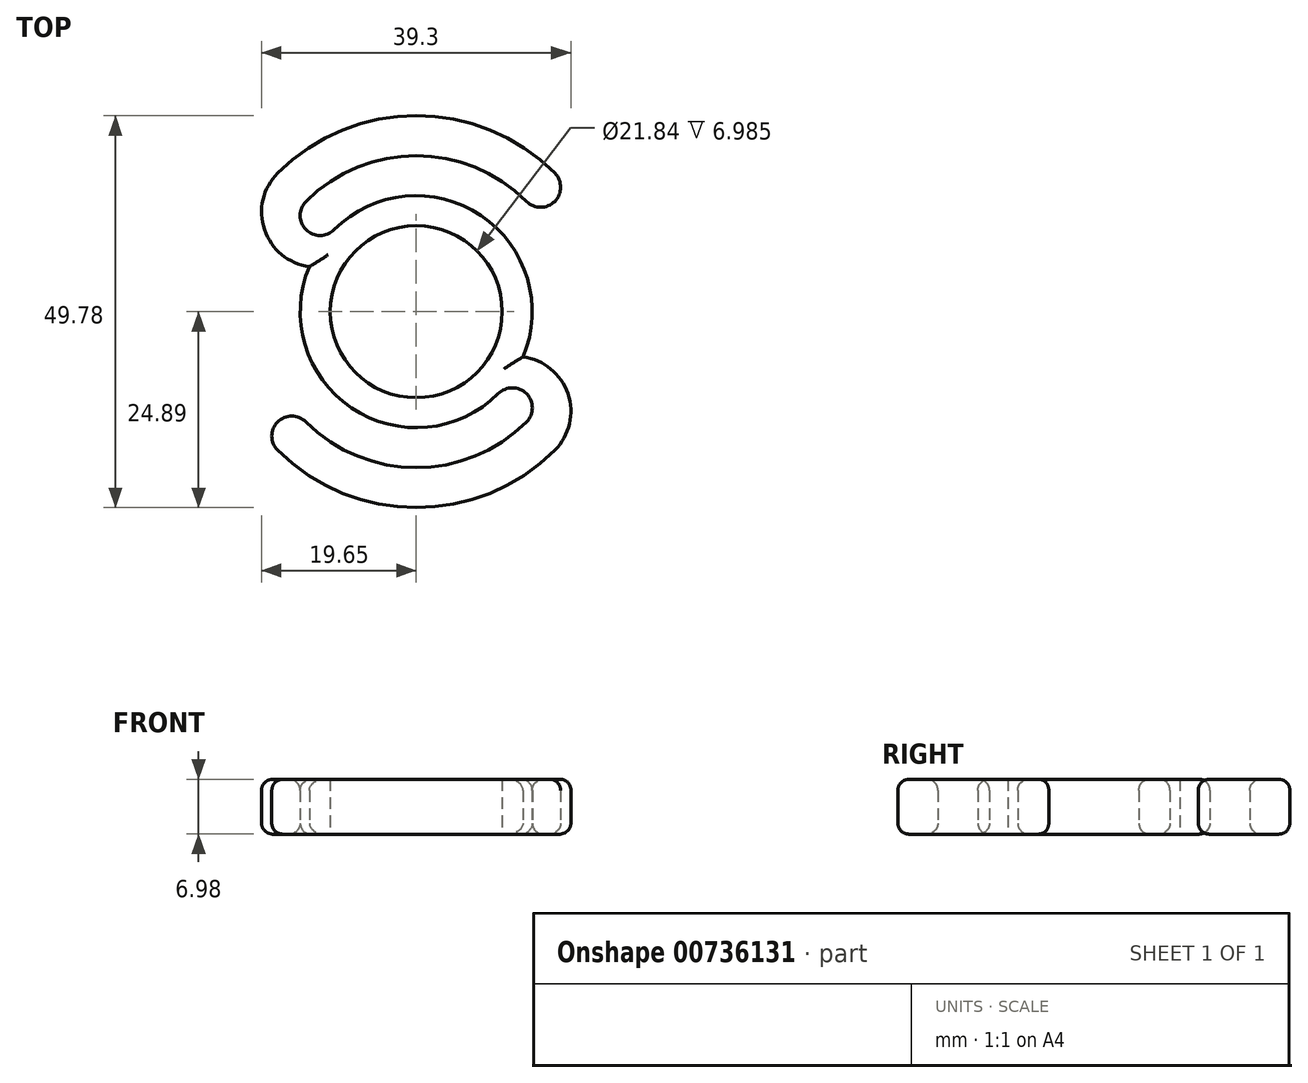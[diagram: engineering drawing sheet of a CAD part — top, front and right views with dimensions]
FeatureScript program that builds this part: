
annotation { "Feature Type Name" : "Feature", "Feature Type Description" : "" }
export const myFeature = defineFeature(function(context is Context, id is Id, definition is map)
    precondition{}
    {
        {
            var Q0;
            Q0=qCreatedBy(makeId("Top.planeOp"),FACE);
            var sketch = newSketch(context, id + "F0", { "sketchPlane" : qUnion([Q0])});
            skCircle(sketch, "E0", {"center": v(0, 0) * mm, "radius": 10.92 * mm});
            skCircle(sketch, "E1", {"center": v(0, 0) * mm, "radius": 24.9 * mm});
            skCircle(sketch, "E2", {"center": v(0, 0) * mm, "radius": 19.81 * mm});
            skLineSegment(sketch, "E3", {"start": v(0, 0) * mm, "end": v(17.6, 17.6) * mm});
            skLineSegment(sketch, "E4", {"start": v(0, 0) * mm, "end": v(-17.6, -17.6) * mm});
            skLineSegment(sketch, "E5", {"start": v(0, 0) * mm, "end": v(-17.6, 17.6) * mm});
            skLineSegment(sketch, "E6", {"start": v(0, 0) * mm, "end": v(17.6, -17.6) * mm});
            skPoint(sketch, "E7", {"position": v(14, 14) * mm});
            skPoint(sketch, "E8", {"position": v(17.6, 17.6) * mm});
            skPoint(sketch, "E9", {"position": v(15.8, 15.8) * mm});
            skCircle(sketch, "E10", {"center": v(15.8, 15.8) * mm, "radius": 2.54 * mm});
            skPoint(sketch, "E11", {"position": v(-17.6, 17.6) * mm});
            skPoint(sketch, "E12", {"position": v(-14, 14) * mm});
            skCircle(sketch, "E13", {"center": v(0, 0) * mm, "radius": 14.73 * mm});
            skPoint(sketch, "E14", {"position": v(-12.66, 12.66) * mm});
            skCircle(sketch, "E15", {"center": v(-12.66, 12.66) * mm, "radius": 6.99 * mm});
            skPoint(sketch, "E16", {"position": v(12.66, -12.66) * mm});
            skPoint(sketch, "E17", {"position": v(-15.8, -15.8) * mm});
            skCircle(sketch, "E18", {"center": v(12.66, -12.66) * mm, "radius": 6.99 * mm});
            skCircle(sketch, "E19", {"center": v(-15.8, -15.8) * mm, "radius": 2.54 * mm});
            skPoint(sketch, "E20", {"position": v(-12.21, 12.21) * mm});
            skCircle(sketch, "E21", {"center": v(-12.21, 12.21) * mm, "radius": 2.54 * mm});
            skPoint(sketch, "E22", {"position": v(12.21, -12.21) * mm});
            skCircle(sketch, "E23", {"center": v(12.21, -12.21) * mm, "radius": 2.54 * mm});
            skSolve(sketch);
        }
        {
            var Q0;
            {var subQ0=sQuery(id+"F0.wireOp",EDGE,"E10");var subQ1=sQuery(id+"F0.wireOp",EDGE,"E3");var subQ2=makeQuery(id+"F0.imprint","INTERSECT",VERTEX,{"derivedFrom":[sQuery(id+"F0.wireOp",EDGE,"E1"),subQ1,subQ0]});Q0=makeQuery(id+"F0.imprint","IMPRINT",FACE,{"disambiguationData":[TD([[makeQuery(id+"F0.imprint","IMPRINT",EDGE,{"disambiguationData":[TD([[subQ2,1.0]])],"derivedFrom":subQ1}),-1.0]])]});}
            var Q1;
            {var subQ0=sQuery(id+"F0.wireOp",EDGE,"E10");var subQ1=sQuery(id+"F0.wireOp",EDGE,"E3");var subQ2=makeQuery(id+"F0.imprint","INTERSECT",VERTEX,{"derivedFrom":[sQuery(id+"F0.wireOp",EDGE,"E1"),subQ1,subQ0]});Q1=makeQuery(id+"F0.imprint","IMPRINT",FACE,{"disambiguationData":[TD([[makeQuery(id+"F0.imprint","IMPRINT",EDGE,{"disambiguationData":[TD([[subQ2,1.0]])],"derivedFrom":subQ1}),1.0]])]});}
            var Q2;
            {var subQ4=sQuery(id+"F0.wireOp",EDGE,"E15");var subQ6=sQuery(id+"F0.wireOp",EDGE,"E2");var subQ7=makeQuery(id+"F0.imprint","INTERSECT",VERTEX,{"disambiguationData":[OD(0.0)],"derivedFrom":[subQ6,subQ4]});Q2=makeQuery(id+"F0.imprint","IMPRINT",FACE,{"disambiguationData":[TD([[makeQuery(id+"F0.imprint","IMPRINT",EDGE,{"disambiguationData":[TD([[subQ7,1.0]])],"derivedFrom":subQ6}),-1.0]])]});}
            var Q3;
            {var subQ0=sQuery(id+"F0.wireOp",EDGE,"E15");var subQ1=sQuery(id+"F0.wireOp",EDGE,"E2");var subQ2=makeQuery(id+"F0.imprint","INTERSECT",VERTEX,{"disambiguationData":[OD(0.0)],"derivedFrom":[subQ1,subQ0]});Q3=makeQuery(id+"F0.imprint","IMPRINT",FACE,{"disambiguationData":[TD([[makeQuery(id+"F0.imprint","IMPRINT",EDGE,{"disambiguationData":[TD([[subQ2,-1.0]])],"derivedFrom":subQ1}),-1.0]])]});}
            var Q4;
            {var subQ0=sQuery(id+"F0.wireOp",EDGE,"E15");var subQ1=sQuery(id+"F0.wireOp",EDGE,"E2");var subQ2=makeQuery(id+"F0.imprint","INTERSECT",VERTEX,{"disambiguationData":[OD(1.0)],"derivedFrom":[subQ1,subQ0]});Q4=makeQuery(id+"F0.imprint","IMPRINT",FACE,{"disambiguationData":[TD([[makeQuery(id+"F0.imprint","IMPRINT",EDGE,{"disambiguationData":[TD([[subQ2,1.0]])],"derivedFrom":subQ1}),-1.0]])]});}
            var Q5;
            {var subQ0=sQuery(id+"F0.wireOp",EDGE,"E15");var subQ1=sQuery(id+"F0.wireOp",EDGE,"E2");var subQ2=makeQuery(id+"F0.imprint","INTERSECT",VERTEX,{"disambiguationData":[OD(1.0)],"derivedFrom":[subQ1,subQ0]});Q5=makeQuery(id+"F0.imprint","IMPRINT",FACE,{"disambiguationData":[TD([[makeQuery(id+"F0.imprint","IMPRINT",EDGE,{"disambiguationData":[TD([[subQ2,-1.0]])],"derivedFrom":subQ0}),1.0]])]});}
            var Q6;
            {var subQ0=sQuery(id+"F0.wireOp",EDGE,"E15");var subQ3=sQuery(id+"F0.wireOp",EDGE,"E13");var subQ5=makeQuery(id+"F0.imprint","INTERSECT",VERTEX,{"disambiguationData":[OD(1.0)],"derivedFrom":[subQ3,subQ0]});Q6=makeQuery(id+"F0.imprint","IMPRINT",FACE,{"disambiguationData":[TD([[makeQuery(id+"F0.imprint","IMPRINT",EDGE,{"disambiguationData":[TD([[subQ5,1.0]])],"derivedFrom":subQ3}),1.0]])]});}
            var Q7;
            {var subQ0=sQuery(id+"F0.wireOp",EDGE,"E15");var subQ3=sQuery(id+"F0.wireOp",EDGE,"E13");var subQ5=makeQuery(id+"F0.imprint","INTERSECT",VERTEX,{"disambiguationData":[OD(0.0)],"derivedFrom":[subQ3,subQ0]});Q7=makeQuery(id+"F0.imprint","IMPRINT",FACE,{"disambiguationData":[TD([[makeQuery(id+"F0.imprint","IMPRINT",EDGE,{"disambiguationData":[TD([[subQ5,-1.0]])],"derivedFrom":subQ3}),1.0]])]});}
            var Q8;
            {var subQ0=sQuery(id+"F0.wireOp",EDGE,"E3");var subQ1=sQuery(id+"F0.wireOp",EDGE,"E0");var subQ2=makeQuery(id+"F0.imprint","INTERSECT",VERTEX,{"derivedFrom":[subQ1,subQ0]});Q8=makeQuery(id+"F0.imprint","IMPRINT",FACE,{"disambiguationData":[TD([[makeQuery(id+"F0.imprint","IMPRINT",EDGE,{"disambiguationData":[TD([[subQ2,-1.0]])],"derivedFrom":subQ0}),1.0]])]});}
            var Q9;
            {var subQ0=sQuery(id+"F0.wireOp",EDGE,"E3");var subQ1=sQuery(id+"F0.wireOp",EDGE,"E0");var subQ2=makeQuery(id+"F0.imprint","INTERSECT",VERTEX,{"derivedFrom":[subQ1,subQ0]});Q9=makeQuery(id+"F0.imprint","IMPRINT",FACE,{"disambiguationData":[TD([[makeQuery(id+"F0.imprint","IMPRINT",EDGE,{"disambiguationData":[TD([[subQ2,-1.0]])],"derivedFrom":subQ0}),-1.0]])]});}
            var Q10;
            {var subQ0=sQuery(id+"F0.wireOp",EDGE,"E4");var subQ1=sQuery(id+"F0.wireOp",EDGE,"E0");var subQ2=makeQuery(id+"F0.imprint","INTERSECT",VERTEX,{"derivedFrom":[subQ1,subQ0]});Q10=makeQuery(id+"F0.imprint","IMPRINT",FACE,{"disambiguationData":[TD([[makeQuery(id+"F0.imprint","IMPRINT",EDGE,{"disambiguationData":[TD([[subQ2,-1.0]])],"derivedFrom":subQ0}),-1.0]])]});}
            var Q11;
            {var subQ0=sQuery(id+"F0.wireOp",EDGE,"E4");var subQ1=sQuery(id+"F0.wireOp",EDGE,"E0");var subQ2=makeQuery(id+"F0.imprint","INTERSECT",VERTEX,{"derivedFrom":[subQ1,subQ0]});Q11=makeQuery(id+"F0.imprint","IMPRINT",FACE,{"disambiguationData":[TD([[makeQuery(id+"F0.imprint","IMPRINT",EDGE,{"disambiguationData":[TD([[subQ2,-1.0]])],"derivedFrom":subQ0}),1.0]])]});}
            var Q12;
            {var subQ0=sQuery(id+"F0.wireOp",EDGE,"E18");var subQ3=sQuery(id+"F0.wireOp",EDGE,"E13");var subQ5=makeQuery(id+"F0.imprint","INTERSECT",VERTEX,{"disambiguationData":[OD(0.0)],"derivedFrom":[subQ3,subQ0]});Q12=makeQuery(id+"F0.imprint","IMPRINT",FACE,{"disambiguationData":[TD([[makeQuery(id+"F0.imprint","IMPRINT",EDGE,{"disambiguationData":[TD([[subQ5,-1.0]])],"derivedFrom":subQ3}),1.0]])]});}
            var Q13;
            {var subQ0=sQuery(id+"F0.wireOp",EDGE,"E18");var subQ3=sQuery(id+"F0.wireOp",EDGE,"E13");var subQ5=makeQuery(id+"F0.imprint","INTERSECT",VERTEX,{"disambiguationData":[OD(1.0)],"derivedFrom":[subQ3,subQ0]});Q13=makeQuery(id+"F0.imprint","IMPRINT",FACE,{"disambiguationData":[TD([[makeQuery(id+"F0.imprint","IMPRINT",EDGE,{"disambiguationData":[TD([[subQ5,1.0]])],"derivedFrom":subQ3}),1.0]])]});}
            var Q14;
            {var subQ0=sQuery(id+"F0.wireOp",EDGE,"E18");var subQ1=sQuery(id+"F0.wireOp",EDGE,"E2");var subQ2=makeQuery(id+"F0.imprint","INTERSECT",VERTEX,{"disambiguationData":[OD(1.0)],"derivedFrom":[subQ1,subQ0]});Q14=makeQuery(id+"F0.imprint","IMPRINT",FACE,{"disambiguationData":[TD([[makeQuery(id+"F0.imprint","IMPRINT",EDGE,{"disambiguationData":[TD([[subQ2,-1.0]])],"derivedFrom":subQ0}),1.0]])]});}
            var Q15;
            {var subQ0=sQuery(id+"F0.wireOp",EDGE,"E18");var subQ1=sQuery(id+"F0.wireOp",EDGE,"E2");var subQ2=makeQuery(id+"F0.imprint","INTERSECT",VERTEX,{"disambiguationData":[OD(1.0)],"derivedFrom":[subQ1,subQ0]});Q15=makeQuery(id+"F0.imprint","IMPRINT",FACE,{"disambiguationData":[TD([[makeQuery(id+"F0.imprint","IMPRINT",EDGE,{"disambiguationData":[TD([[subQ2,1.0]])],"derivedFrom":subQ1}),-1.0]])]});}
            var Q16;
            {var subQ0=sQuery(id+"F0.wireOp",EDGE,"E18");var subQ1=sQuery(id+"F0.wireOp",EDGE,"E2");var subQ2=makeQuery(id+"F0.imprint","INTERSECT",VERTEX,{"disambiguationData":[OD(0.0)],"derivedFrom":[subQ1,subQ0]});Q16=makeQuery(id+"F0.imprint","IMPRINT",FACE,{"disambiguationData":[TD([[makeQuery(id+"F0.imprint","IMPRINT",EDGE,{"disambiguationData":[TD([[subQ2,-1.0]])],"derivedFrom":subQ1}),-1.0]])]});}
            var Q17;
            {var subQ0=sQuery(id+"F0.wireOp",EDGE,"E19");var subQ1=sQuery(id+"F0.wireOp",EDGE,"E4");var subQ2=makeQuery(id+"F0.imprint","INTERSECT",VERTEX,{"derivedFrom":[sQuery(id+"F0.wireOp",EDGE,"E1"),subQ1,subQ0]});Q17=makeQuery(id+"F0.imprint","IMPRINT",FACE,{"disambiguationData":[TD([[makeQuery(id+"F0.imprint","IMPRINT",EDGE,{"disambiguationData":[TD([[subQ2,1.0]])],"derivedFrom":subQ1}),1.0]])]});}
            var Q18;
            {var subQ4=sQuery(id+"F0.wireOp",EDGE,"E18");var subQ6=sQuery(id+"F0.wireOp",EDGE,"E2");var subQ7=makeQuery(id+"F0.imprint","INTERSECT",VERTEX,{"disambiguationData":[OD(0.0)],"derivedFrom":[subQ6,subQ4]});Q18=makeQuery(id+"F0.imprint","IMPRINT",FACE,{"disambiguationData":[TD([[makeQuery(id+"F0.imprint","IMPRINT",EDGE,{"disambiguationData":[TD([[subQ7,1.0]])],"derivedFrom":subQ6}),-1.0]])]});}
            var Q19;
            {var subQ0=sQuery(id+"F0.wireOp",EDGE,"E19");var subQ1=sQuery(id+"F0.wireOp",EDGE,"E4");var subQ2=makeQuery(id+"F0.imprint","INTERSECT",VERTEX,{"derivedFrom":[sQuery(id+"F0.wireOp",EDGE,"E1"),subQ1,subQ0]});Q19=makeQuery(id+"F0.imprint","IMPRINT",FACE,{"disambiguationData":[TD([[makeQuery(id+"F0.imprint","IMPRINT",EDGE,{"disambiguationData":[TD([[subQ2,1.0]])],"derivedFrom":subQ1}),-1.0]])]});}
            extrude(context, id + "F1", {"entities" : qUnion([Q0, Q1, Q2, Q3, Q4, Q5, Q6, Q7, Q8, Q9, Q10, Q11, Q12, Q13, Q14, Q15, Q16, Q17, Q18, Q19]), "endBound" : BoundingType.SYMMETRIC, "depth" : 7 * mm, "offsetDistance" : 25.4 * mm});
        }
        {
            var Q0;
            {var subQ0=sQuery(id+"F0.wireOp",EDGE,"E1");Q0=makeQuery(id+"F1.opExtrude","CAP_EDGE",EDGE,{"disambiguationData":[OSD([subQ0]),TDD([makeQuery(id+"F0.imprint","IMPRINT",EDGE,{"disambiguationData":[TD([[makeQuery(id+"F0.imprint","INTERSECT",VERTEX,{"derivedFrom":[subQ0,sQuery(id+"F0.wireOp",EDGE,"E3"),sQuery(id+"F0.wireOp",EDGE,"E10")]}),-1.0]])],"derivedFrom":subQ0})])],"isStart":false});}
            var Q1;
            Q1=makeQuery(id+"F1.opExtrude","CAP_EDGE",EDGE,{"disambiguationData":[OSD([sQuery(id+"F0.wireOp",EDGE,"E15")])],"isStart":false});
            var Q2;
            {var subQ0=sQuery(id+"F0.wireOp",EDGE,"E13");var subQ1=makeQuery(id+"F0.imprint","INTERSECT",VERTEX,{"disambiguationData":[OD(0.0)],"derivedFrom":[subQ0,sQuery(id+"F0.wireOp",EDGE,"E18")]});var subQ2=makeQuery(id+"F0.imprint","INTERSECT",VERTEX,{"derivedFrom":[sQuery(id+"F0.wireOp",EDGE,"E4"),subQ0]});Q2=makeQuery(id+"F1.opExtrude","CAP_EDGE",EDGE,{"disambiguationData":[OSD([subQ0]),TDD([makeQuery(id+"F0.imprint","IMPRINT",EDGE,{"disambiguationData":[TD([[subQ2,1.0]])],"derivedFrom":subQ0}),makeQuery(id+"F0.imprint","IMPRINT",EDGE,{"disambiguationData":[TD([[subQ2,-1.0]])],"derivedFrom":subQ0}),makeQuery(id+"F0.imprint","IMPRINT",EDGE,{"disambiguationData":[TD([[subQ1,-1.0]])],"derivedFrom":subQ0})])],"isStart":false});}
            var Q3;
            {var subQ0=sQuery(id+"F0.wireOp",EDGE,"E13");var subQ1=makeQuery(id+"F0.imprint","INTERSECT",VERTEX,{"derivedFrom":[sQuery(id+"F0.wireOp",EDGE,"E3"),subQ0]});var subQ2=makeQuery(id+"F0.imprint","INTERSECT",VERTEX,{"disambiguationData":[OD(0.0)],"derivedFrom":[subQ0,sQuery(id+"F0.wireOp",EDGE,"E15")]});Q3=makeQuery(id+"F1.opExtrude","CAP_EDGE",EDGE,{"disambiguationData":[OSD([subQ0]),TDD([makeQuery(id+"F0.imprint","IMPRINT",EDGE,{"disambiguationData":[TD([[subQ1,-1.0]])],"derivedFrom":subQ0}),makeQuery(id+"F0.imprint","IMPRINT",EDGE,{"disambiguationData":[TD([[subQ2,-1.0]])],"derivedFrom":subQ0}),makeQuery(id+"F0.imprint","IMPRINT",EDGE,{"disambiguationData":[TD([[subQ1,1.0]])],"derivedFrom":subQ0})])],"isStart":false});}
            var Q4;
            Q4=makeQuery(id+"F1.opExtrude","CAP_EDGE",EDGE,{"disambiguationData":[OSD([sQuery(id+"F0.wireOp",EDGE,"E21")])],"isStart":false});
            var Q5;
            {var subQ0=sQuery(id+"F0.wireOp",EDGE,"E2");var subQ1=makeQuery(id+"F0.imprint","INTERSECT",VERTEX,{"disambiguationData":[OD(0.0)],"derivedFrom":[subQ0,sQuery(id+"F0.wireOp",EDGE,"E15")]});Q5=makeQuery(id+"F1.opExtrude","CAP_EDGE",EDGE,{"disambiguationData":[OSD([subQ0]),TDD([makeQuery(id+"F0.imprint","IMPRINT",EDGE,{"disambiguationData":[TD([[subQ1,1.0]])],"derivedFrom":subQ0}),makeQuery(id+"F0.imprint","IMPRINT",EDGE,{"disambiguationData":[TD([[subQ1,-1.0]])],"derivedFrom":subQ0})])],"isStart":false});}
            var Q6;
            Q6=makeQuery(id+"F1.opExtrude","CAP_EDGE",EDGE,{"disambiguationData":[OSD([sQuery(id+"F0.wireOp",EDGE,"E10")])],"isStart":false});
            var Q7;
            Q7=makeQuery(id+"F1.opExtrude","CAP_EDGE",EDGE,{"disambiguationData":[OSD([sQuery(id+"F0.wireOp",EDGE,"E18")])],"isStart":false});
            var Q8;
            Q8=makeQuery(id+"F1.opExtrude","CAP_EDGE",EDGE,{"disambiguationData":[OSD([sQuery(id+"F0.wireOp",EDGE,"E23")])],"isStart":false});
            var Q9;
            {var subQ0=sQuery(id+"F0.wireOp",EDGE,"E2");var subQ1=makeQuery(id+"F0.imprint","INTERSECT",VERTEX,{"disambiguationData":[OD(0.0)],"derivedFrom":[subQ0,sQuery(id+"F0.wireOp",EDGE,"E18")]});Q9=makeQuery(id+"F1.opExtrude","CAP_EDGE",EDGE,{"disambiguationData":[OSD([subQ0]),TDD([makeQuery(id+"F0.imprint","IMPRINT",EDGE,{"disambiguationData":[TD([[subQ1,1.0]])],"derivedFrom":subQ0}),makeQuery(id+"F0.imprint","IMPRINT",EDGE,{"disambiguationData":[TD([[subQ1,-1.0]])],"derivedFrom":subQ0})])],"isStart":false});}
            var Q10;
            Q10=makeQuery(id+"F1.opExtrude","CAP_EDGE",EDGE,{"disambiguationData":[OSD([sQuery(id+"F0.wireOp",EDGE,"E19")])],"isStart":false});
            var Q11;
            {var subQ0=sQuery(id+"F0.wireOp",EDGE,"E1");Q11=makeQuery(id+"F1.opExtrude","CAP_EDGE",EDGE,{"disambiguationData":[OSD([subQ0]),TDD([makeQuery(id+"F0.imprint","IMPRINT",EDGE,{"disambiguationData":[TD([[makeQuery(id+"F0.imprint","INTERSECT",VERTEX,{"derivedFrom":[subQ0,sQuery(id+"F0.wireOp",EDGE,"E4"),sQuery(id+"F0.wireOp",EDGE,"E19")]}),-1.0]])],"derivedFrom":subQ0})])],"isStart":false});}
            var Q12;
            Q12=makeQuery(id+"F1.opExtrude","CAP_EDGE",EDGE,{"disambiguationData":[OSD([sQuery(id+"F0.wireOp",EDGE,"E10")])],"isStart":true});
            var Q13;
            {var subQ0=sQuery(id+"F0.wireOp",EDGE,"E1");Q13=makeQuery(id+"F1.opExtrude","CAP_EDGE",EDGE,{"disambiguationData":[OSD([subQ0]),TDD([makeQuery(id+"F0.imprint","IMPRINT",EDGE,{"disambiguationData":[TD([[makeQuery(id+"F0.imprint","INTERSECT",VERTEX,{"derivedFrom":[subQ0,sQuery(id+"F0.wireOp",EDGE,"E3"),sQuery(id+"F0.wireOp",EDGE,"E10")]}),-1.0]])],"derivedFrom":subQ0})])],"isStart":true});}
            var Q14;
            {var subQ0=sQuery(id+"F0.wireOp",EDGE,"E13");var subQ1=makeQuery(id+"F0.imprint","INTERSECT",VERTEX,{"disambiguationData":[OD(0.0)],"derivedFrom":[subQ0,sQuery(id+"F0.wireOp",EDGE,"E18")]});var subQ2=makeQuery(id+"F0.imprint","INTERSECT",VERTEX,{"derivedFrom":[sQuery(id+"F0.wireOp",EDGE,"E4"),subQ0]});Q14=makeQuery(id+"F1.opExtrude","CAP_EDGE",EDGE,{"disambiguationData":[OSD([subQ0]),TDD([makeQuery(id+"F0.imprint","IMPRINT",EDGE,{"disambiguationData":[TD([[subQ2,1.0]])],"derivedFrom":subQ0}),makeQuery(id+"F0.imprint","IMPRINT",EDGE,{"disambiguationData":[TD([[subQ2,-1.0]])],"derivedFrom":subQ0}),makeQuery(id+"F0.imprint","IMPRINT",EDGE,{"disambiguationData":[TD([[subQ1,-1.0]])],"derivedFrom":subQ0})])],"isStart":true});}
            fillet(context, id + "F2", {"entities" : qUnion([Q0, Q1, Q2, Q3, Q4, Q5, Q6, Q7, Q8, Q9, Q10, Q11, Q12, Q13, Q14]), "radius" : 1.4 * mm, "tangentPropagation" : true, "allowEdgeOverflow" : false});
        }
    });
